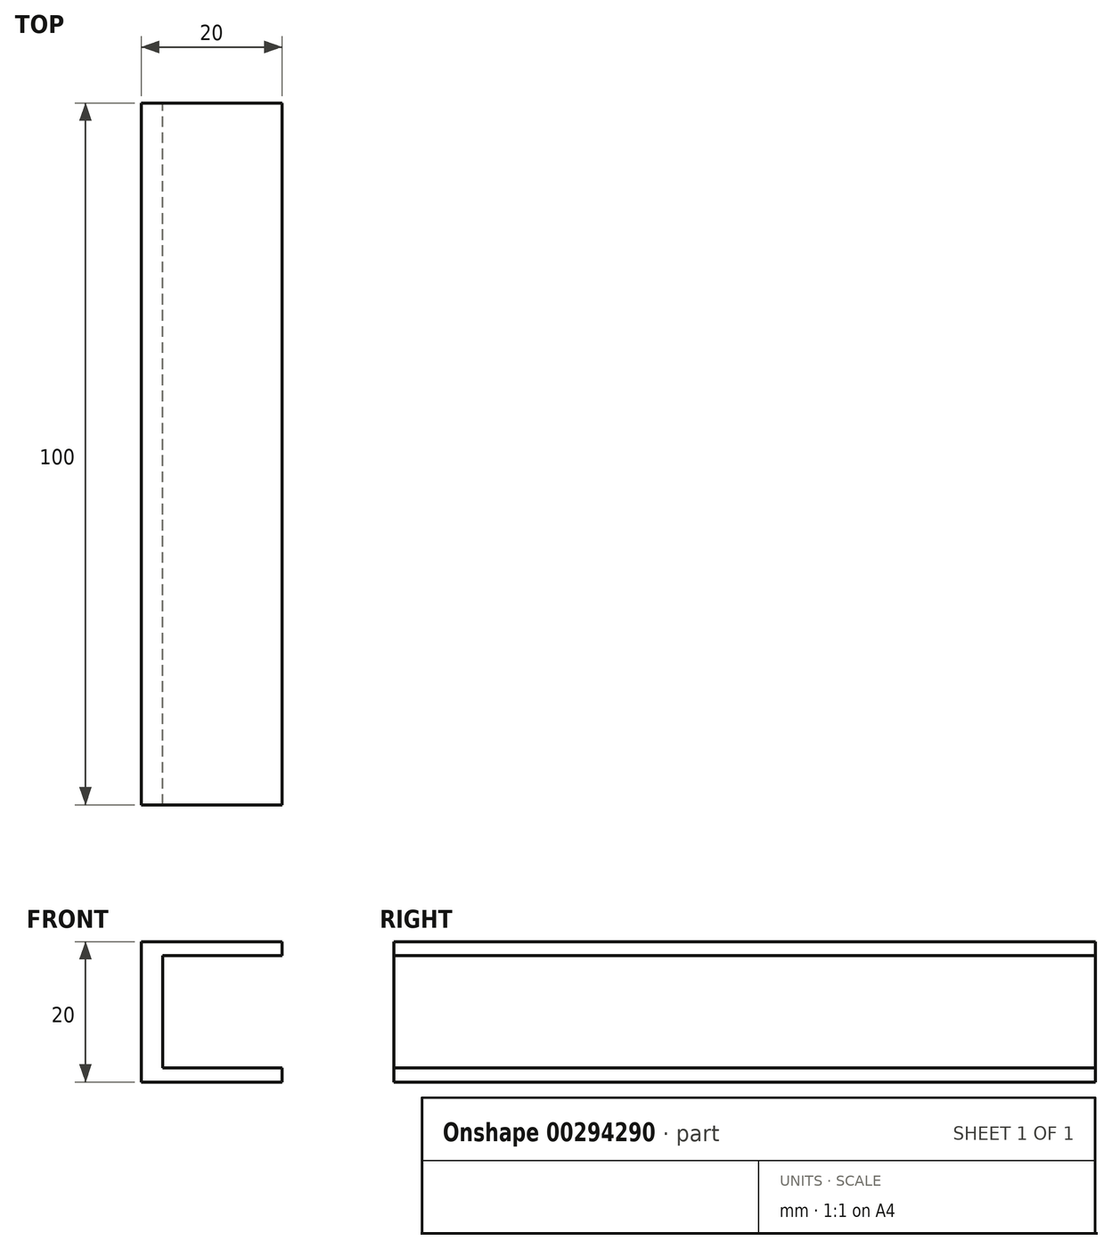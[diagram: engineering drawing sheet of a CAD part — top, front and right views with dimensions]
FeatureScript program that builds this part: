
annotation { "Feature Type Name" : "Feature", "Feature Type Description" : "" }
export const myFeature = defineFeature(function(context is Context, id is Id, definition is map)
    precondition{}
    {
        {
            var Q0;
            Q0=qCreatedBy(makeId("Front.planeOp"),FACE);
            var sketch = newSketch(context, id + "F0", { "sketchPlane" : qUnion([Q0])});
            skLineSegment(sketch, "E0", {"start": v(0, 0) * mm, "end": v(-20, 0) * mm});
            skLineSegment(sketch, "E1", {"start": v(-20, 0) * mm, "end": v(-20, 20) * mm});
            skLineSegment(sketch, "E2", {"start": v(-20, 20) * mm, "end": v(0, 20) * mm});
            skLineSegment(sketch, "E3", {"start": v(0, 20) * mm, "end": v(0, 18) * mm});
            skLineSegment(sketch, "E4", {"start": v(0, 18) * mm, "end": v(-17, 18) * mm});
            skLineSegment(sketch, "E5", {"start": v(-17, 18) * mm, "end": v(-17, 2) * mm});
            skLineSegment(sketch, "E6", {"start": v(-17, 2) * mm, "end": v(0, 2) * mm});
            skLineSegment(sketch, "E7", {"start": v(0, 2) * mm, "end": v(0, 0) * mm});
            skSolve(sketch);
        }
        {
            var Q0;
            Q0 = qSketchRegion(id + "F0", true);
            extrude(context, id + "F1", {"entities" : qUnion([Q0]), "depth" : 100 * mm});
        }
    });
